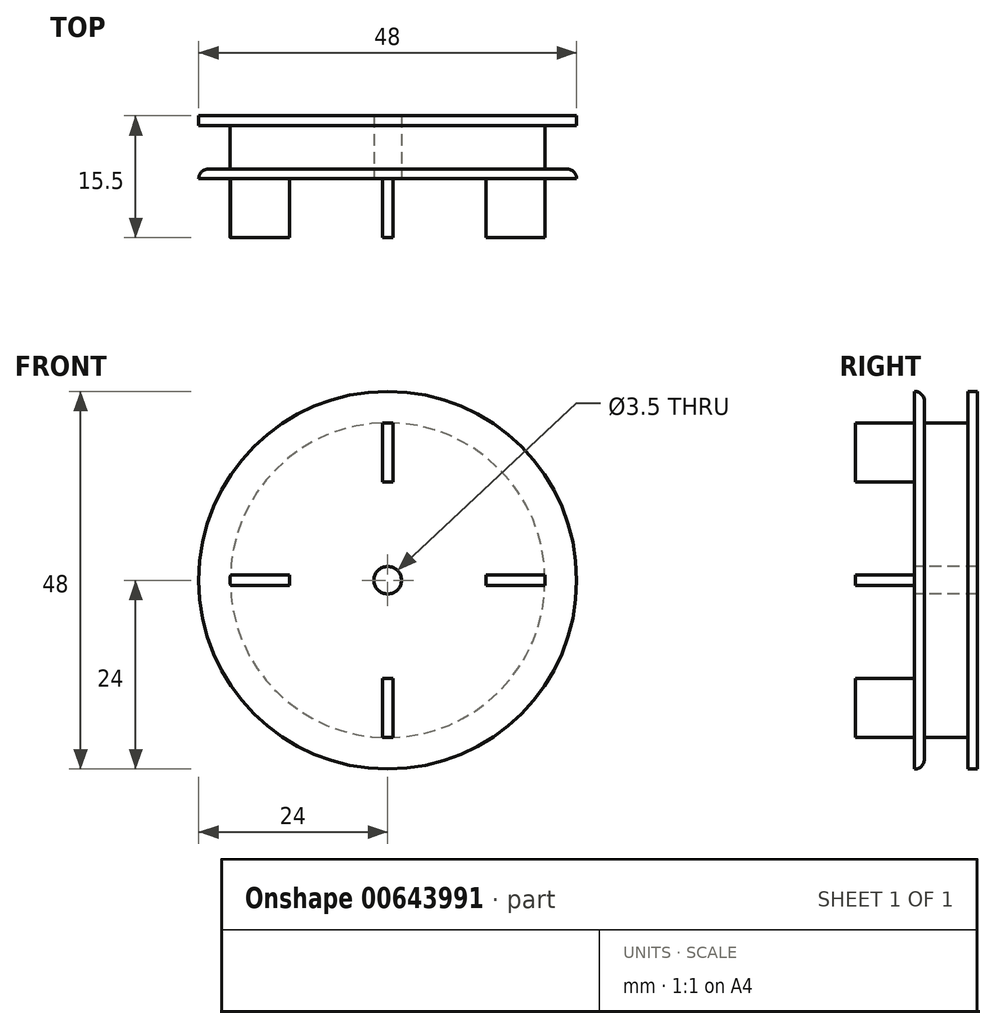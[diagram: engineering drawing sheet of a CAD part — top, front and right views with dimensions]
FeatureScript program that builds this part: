
annotation { "Feature Type Name" : "Feature", "Feature Type Description" : "" }
export const myFeature = defineFeature(function(context is Context, id is Id, definition is map)
    precondition{}
    {
        {
            var Q0;
            Q0=qCreatedBy(makeId("Front.planeOp"),FACE);
            var sketch = newSketch(context, id + "F0", { "sketchPlane" : qUnion([Q0])});
            skCircle(sketch, "E0", {"center": v(0, 0) * mm, "radius": 20 * mm});
            skPoint(sketch, "E1", {"position": v(0, 20) * mm});
            skPoint(sketch, "E2", {"position": v(0, -20) * mm});
            skPoint(sketch, "E3", {"position": v(20, 0) * mm});
            skPoint(sketch, "E4", {"position": v(-20, 0) * mm});
            skPoint(sketch, "E5", {"position": v(-0.65, 19.99) * mm});
            skPoint(sketch, "E6", {"position": v(0.65, 19.99) * mm});
            skLineSegment(sketch, "E7", {"start": v(-0.65, 19.99) * mm, "end": v(-0.65, 12.5) * mm});
            skLineSegment(sketch, "E8", {"start": v(-0.65, 12.5) * mm, "end": v(0.65, 12.5) * mm});
            skLineSegment(sketch, "E9", {"start": v(0.65, 12.5) * mm, "end": v(0.65, 19.99) * mm});
            skLineSegment(sketch, "E10.1.0", {"start": v(-12.5, -0.65) * mm, "end": v(-12.5, 0.65) * mm});
            skLineSegment(sketch, "E10.1.1", {"start": v(-12.5, 0.65) * mm, "end": v(-19.99, 0.65) * mm});
            skLineSegment(sketch, "E10.1.3", {"start": v(-19.99, -0.65) * mm, "end": v(-12.5, -0.65) * mm});
            skPoint(sketch, "E10.1.4", {"position": v(-19.99, -0.65) * mm});
            skPoint(sketch, "E10.1.5", {"position": v(-19.99, 0.65) * mm});
            skLineSegment(sketch, "E10.2.0", {"start": v(0.65, -12.5) * mm, "end": v(-0.65, -12.5) * mm});
            skLineSegment(sketch, "E10.2.1", {"start": v(-0.65, -12.5) * mm, "end": v(-0.65, -19.99) * mm});
            skLineSegment(sketch, "E10.2.3", {"start": v(0.65, -19.99) * mm, "end": v(0.65, -12.5) * mm});
            skPoint(sketch, "E10.2.4", {"position": v(0.65, -19.99) * mm});
            skPoint(sketch, "E10.2.5", {"position": v(-0.65, -19.99) * mm});
            skLineSegment(sketch, "E10.3.0", {"start": v(12.5, 0.65) * mm, "end": v(12.5, -0.65) * mm});
            skLineSegment(sketch, "E10.3.1", {"start": v(12.5, -0.65) * mm, "end": v(19.99, -0.65) * mm});
            skLineSegment(sketch, "E10.3.3", {"start": v(19.99, 0.65) * mm, "end": v(12.5, 0.65) * mm});
            skPoint(sketch, "E10.3.4", {"position": v(19.99, 0.65) * mm});
            skPoint(sketch, "E10.3.5", {"position": v(19.99, -0.65) * mm});
            skCircle(sketch, "E11", {"center": v(0, 0) * mm, "radius": 24 * mm});
            skPoint(sketch, "E12", {"position": v(0, 24) * mm});
            skCircle(sketch, "E13", {"center": v(0, 0) * mm, "radius": 1.75 * mm});
            skSolve(sketch);
        }
        {
            var Q0;
            {var subQ2=sQuery(id+"F0.wireOp",EDGE,"E7");Q0=makeQuery(id+"F0.imprint","IMPRINT",FACE,{"disambiguationData":[TD([[makeQuery(id+"F0.imprint","IMPRINT",EDGE,{"derivedFrom":subQ2}),-1.0]])]});}
            var Q1;
            {var subQ0=sQuery(id+"F0.wireOp",EDGE,"E7");Q1=makeQuery(id+"F0.imprint","IMPRINT",FACE,{"disambiguationData":[TD([[makeQuery(id+"F0.imprint","IMPRINT",EDGE,{"derivedFrom":subQ0}),1.0]])]});}
            var Q2;
            Q2=makeQuery(id+"F0.imprint","IMPRINT",FACE,{"disambiguationData":[TD([[makeQuery(id+"F0.imprint","IMPRINT",EDGE,{"derivedFrom":sQuery(id+"F0.wireOp",EDGE,"E10.3.0")}),1.0]])]});
            var Q3;
            Q3=makeQuery(id+"F0.imprint","IMPRINT",FACE,{"disambiguationData":[TD([[makeQuery(id+"F0.imprint","IMPRINT",EDGE,{"derivedFrom":sQuery(id+"F0.wireOp",EDGE,"E10.1.0")}),1.0]])]});
            var Q4;
            Q4=makeQuery(id+"F0.imprint","IMPRINT",FACE,{"disambiguationData":[TD([[makeQuery(id+"F0.imprint","IMPRINT",EDGE,{"derivedFrom":sQuery(id+"F0.wireOp",EDGE,"E10.2.0")}),1.0]])]});
            var Q5;
            Q5=makeQuery(id+"F0.imprint","IMPRINT",FACE,{"disambiguationData":[TD([[makeQuery(id+"F0.imprint","IMPRINT",EDGE,{"derivedFrom":sQuery(id+"F0.wireOp",EDGE,"E11")}),1.0]])]});
            extrude(context, id + "F1", {"entities" : qUnion([Q0, Q1, Q2, Q3, Q4, Q5]), "oppositeDirection" : true, "depth" : 8 * mm, "offsetDistance" : 25 * mm});
        }
        {
            var Q0;
            Q0=makeQuery(id+"F0.imprint","IMPRINT",FACE,{"disambiguationData":[TD([[makeQuery(id+"F0.imprint","IMPRINT",EDGE,{"derivedFrom":sQuery(id+"F0.wireOp",EDGE,"E11")}),1.0]])]});
            extrude(context, id + "F2", {"entities" : qUnion([Q0]), "operationType" : NewBodyOperationType.REMOVE, "oppositeDirection" : true, "depth" : 6.75 * mm, "offsetDistance" : 25 * mm});
        }
        {
            var Q0;
            Q0=makeQuery(id+"F0.imprint","IMPRINT",FACE,{"disambiguationData":[TD([[makeQuery(id+"F0.imprint","IMPRINT",EDGE,{"derivedFrom":sQuery(id+"F0.wireOp",EDGE,"E11")}),1.0]])]});
            extrude(context, id + "F3", {"entities" : qUnion([Q0]), "oppositeDirection" : true, "depth" : 1.25 * mm, "offsetDistance" : 25 * mm});
        }
        {
            var Q0;
            Q0=makeQuery(id+"F2.boolean.opBoolean","COPY",EDGE,{"derivedFrom":makeQuery(id+"F2.opExtrude","CAP_EDGE",EDGE,{"disambiguationData":[OSD([sQuery(id+"F0.wireOp",EDGE,"E11")])],"isStart":false})});
            var Q1;
            Q1=makeQuery(id+"F3.opExtrude","CAP_EDGE",EDGE,{"disambiguationData":[OSD([sQuery(id+"F0.wireOp",EDGE,"E11")])],"isStart":false});
            fillet(context, id + "F4", {"entities" : qUnion([Q0, Q1]), "radius" : 1.25 * mm, "tangentPropagation" : true, "allowEdgeOverflow" : false});
        }
        {
            var Q0;
            {var subQ0=sQuery(id+"F0.wireOp",EDGE,"E7");Q0=makeQuery(id+"F0.imprint","IMPRINT",FACE,{"disambiguationData":[TD([[makeQuery(id+"F0.imprint","IMPRINT",EDGE,{"derivedFrom":subQ0}),1.0]])]});}
            var Q1;
            Q1=makeQuery(id+"F0.imprint","IMPRINT",FACE,{"disambiguationData":[TD([[makeQuery(id+"F0.imprint","IMPRINT",EDGE,{"derivedFrom":sQuery(id+"F0.wireOp",EDGE,"E10.1.0")}),1.0]])]});
            var Q2;
            Q2=makeQuery(id+"F0.imprint","IMPRINT",FACE,{"disambiguationData":[TD([[makeQuery(id+"F0.imprint","IMPRINT",EDGE,{"derivedFrom":sQuery(id+"F0.wireOp",EDGE,"E10.3.0")}),1.0]])]});
            var Q3;
            Q3=makeQuery(id+"F0.imprint","IMPRINT",FACE,{"disambiguationData":[TD([[makeQuery(id+"F0.imprint","IMPRINT",EDGE,{"derivedFrom":sQuery(id+"F0.wireOp",EDGE,"E10.2.0")}),1.0]])]});
            extrude(context, id + "F5", {"entities" : qUnion([Q0, Q1, Q2, Q3]), "operationType" : NewBodyOperationType.ADD, "depth" : 7.5 * mm, "offsetDistance" : 25 * mm});
        }
    });
